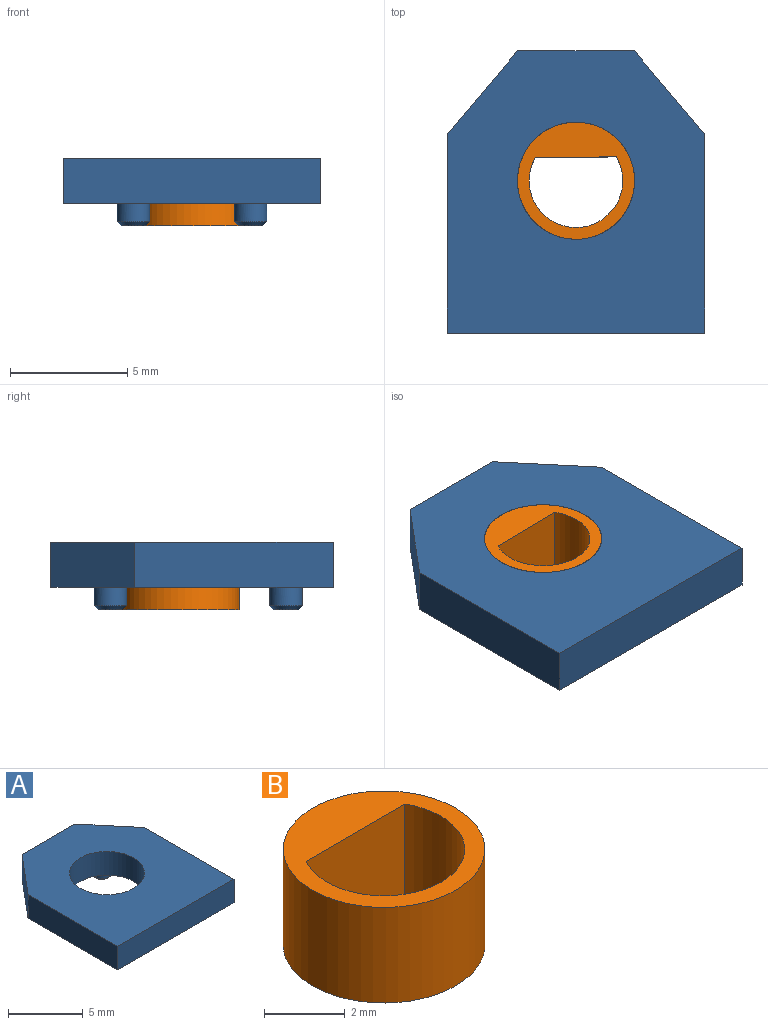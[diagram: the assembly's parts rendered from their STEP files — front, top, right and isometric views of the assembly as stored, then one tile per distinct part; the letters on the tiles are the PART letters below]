
ASSEMBLY  parts=2 mates=1
PART A: 21 faces, bbox 11x12x2.9 mm
  f0: plane 11x1.93mm, normal (0,-1,0), area 21.2mm2, adj f1,f5,f7,f8
  f1: plane 8.46x1.93mm, normal (1,0,0), area 16.3mm2, adj f0,f2,f7,f8
  f2: plane 3.58x3mm, normal (0.77,0.64,0), area 9mm2, adj f1,f3,f7,f8
  f3: plane 4.99x1.93mm, normal (0,1,0), area 9.6mm2, adj f2,f4,f7,f8
  f4: plane 3.58x3mm, normal (-0.77,0.64,0), area 9mm2, adj f3,f5,f7,f8
  f5: plane 8.46x1.93mm, normal (-1,0,0), area 16.3mm2, adj f0,f4,f7,f8
  f6: cylinder r=2.5mm len=5mm, axis (0,0,-1), area 30.3mm2, adj f7,f8
  f7: plane 12.04x11mm, normal (0,0,1), area 102.1mm2, adj f0,f1,f2,f3,f4,f5,f6
  f8: plane 12.04x11mm, normal (0,0,-1), area 95.9mm2, adj f0,f1,f2,f3,f4,f5,f6,f9
  f9: cylinder r=0.7mm len=1.4mm, axis (0,0,1), area 3.5mm2, adj f8,f19
  f10: plane 1.04x1.04mm, normal (0,0,-1), area 0.8mm2, adj f19
  f11: cylinder r=0.7mm len=1.4mm, axis (0,0,1), area 3.5mm2, adj f8,f18
  f12: plane 1.04x1.04mm, normal (0,0,-1), area 0.8mm2, adj f18
  f13: cylinder r=0.7mm len=1.4mm, axis (0,0,1), area 3.5mm2, adj f8,f17
  f14: plane 1.04x1.04mm, normal (0,0,-1), area 0.8mm2, adj f17
  f15: cylinder r=0.7mm len=1.4mm, axis (0,0,1), area 3.5mm2, adj f8,f20
  f16: plane 1.04x1.04mm, normal (0,0,-1), area 0.8mm2, adj f20
  f17: cone r=0.52mm half-angle=45deg, axis (0,0,1), area 1mm2, adj f13,f14
  f18: cone r=0.52mm half-angle=45deg, axis (0,0,1), area 1mm2, adj f11,f12
  f19: cone r=0.52mm half-angle=45deg, axis (0,0,1), area 1mm2, adj f9,f10
  f20: cone r=0.52mm half-angle=45deg, axis (0,0,1), area 1mm2, adj f15,f16
PART B: 5 faces, bbox 5x5x2.9 mm
  f0: cylinder r=2mm len=4mm, axis (0,0,1), area 24.3mm2, adj f1,f3,f4
  f1: plane 3.46x2.9mm, normal (0,-1,0), area 10mm2, adj f0,f3,f4
  f2: cylinder r=2.5mm len=5mm, axis (0,0,1), area 45.6mm2, adj f3,f4
  f3: plane 5x5mm, normal (0,0,-1), area 9.5mm2, adj f0,f1,f2
  f4: plane 5x5mm, normal (0,0,1), area 9.5mm2, adj f0,f1,f2
PLACE A t=(0,0,-1.93)mm
PLACE B rot(axis=(0,0,1),0.7deg) t=(0,0,-1.93)mm
MATE revolute B.f2 <-> A.f6  axis (0,0,1) through (0,0,0)mm
